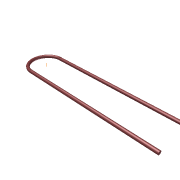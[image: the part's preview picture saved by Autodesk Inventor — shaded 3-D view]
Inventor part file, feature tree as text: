
AUTODESK INVENTOR PART (.ipt)
format: ipt  version: unknown  size: 165,888 bytes
history: native  units: mm
features: sketch x2, sweep x1
ambient origin geometry x8: Origin, YZ Plane, XZ Plane, XY Plane, X Axis, Y Axis, Z Axis, Center Point
feature tree (3):
  sweep  "Sweep1"
  sketch  "Sketch1"  dims[d0=80.0mm d1=20.0mm]
  sketch  "Sketch2"  dims[d2=10.0mm d3=2.0mm d4=0.0mm d5=80.0mm]
